# Revit family: 931-20-001 DN400
name_source: partatom
category: Pipe Accessories
units: mm (PartAtom-declared; Revit-internal decimal feet)

## family parameters
Always vertical = Yes
Cut with Voids When Loaded = No
Part Type = Valve - Breaks Into
Round Connector Dimension = Use Diameter
Shared = No
Work Plane-Based = No

## types (2) — shared parameters
1 = 1 mm  [stored 0.00328084 ft]
2 = 3 mm  [stored 0.00984252 ft]
Actuator_FL_T = 20 mm  [stored 0.0656168 ft]
Actuator_Flange_R = 75 mm  [stored 0.246063 ft]
B = 195 mm  [stored 0.639764 ft]
B1 = 196 mm  [stored 0.643045 ft]
Body_Thickness = 2 mm  [stored 0.00656168 ft]
Body_dim = 38 mm  [stored 0.124672 ft]
Body_dim1 = 71 mm
Body_thickness = 206 mm
Bore_R = 200 mm  [stored 0.656168 ft]
C = 102 mm  [stored 0.334646 ft]
D = 242 mm  [stored 0.793963 ft]
DN = 400 mm  [stored 1.31234 ft]
DN400_PN10 = 931-400-20-010020200000
DN400_PN16 = 931-400-20-020020200000
Description_ = AVK BUTTERFLY VALVE, LUG, PN10/16
E = 328 mm  [stored 1.07612 ft]
F = 43 mm  [stored 0.141076 ft]
G = 27 mm  [stored 0.0885827 ft]
H = 88 mm
Hole = 30 mm  [stored 0.0984252 ft]
Hole1 = 21 mm  [stored 0.0688976 ft]
Search_table = 931-20-001 DN400
Slot_dim = 28 mm  [stored 0.0918635 ft]
URL_product_pages = https://www.avkvalves.com
base = 36 mm  [stored 0.11811 ft]
base1 = 20 mm  [stored 0.0656168 ft]
base_dis = 286 mm
disk1 = 27 mm  [stored 0.0885827 ft]
disk11 = 35 mm  [stored 0.114829 ft]
disk2 = 390 mm  [stored 1.27953 ft]
hole1 = 14 mm  [stored 0.0459318 ft]
rubber = 21 mm  [stored 0.0688976 ft]
support = 292 mm  [stored 0.958005 ft]
wafer = 113 mm
wafer_F = 40 mm  [stored 0.131234 ft]
wafer_dim2 = 113 mm
wafer_fillet = 56 mm  [stored 0.183727 ft]
zero-valued in all types: DISK, Default Elevation

## per-type parameters (varying)
| type | Flange_R | Flange_T | PCD_R | disk | disk22 | wafer_dim1 |
| DN400_PN10 | 228 mm  [stored 0.748031 ft] | 25 mm  [stored 0.082021 ft] | 258 mm | 15 mm  [stored 0.0492126 ft] | 20 mm  [stored 0.0656168 ft] | 25 mm  [stored 0.082021 ft] |
| DN400_PN16 | 230 mm  [stored 0.754593 ft] | 28 mm  [stored 0.0918635 ft] | 263 mm | 16 mm  [stored 0.0524934 ft] | 21 mm  [stored 0.0688976 ft] | 28 mm  [stored 0.0918635 ft] |

note: [stored X ft] marks values corroborated as IEEE doubles in the binary element streams (Revit-internal decimal feet)

## geometry (parser evidence)
native form markers: Sweep x4
no freeform markers — native parametric forms only
